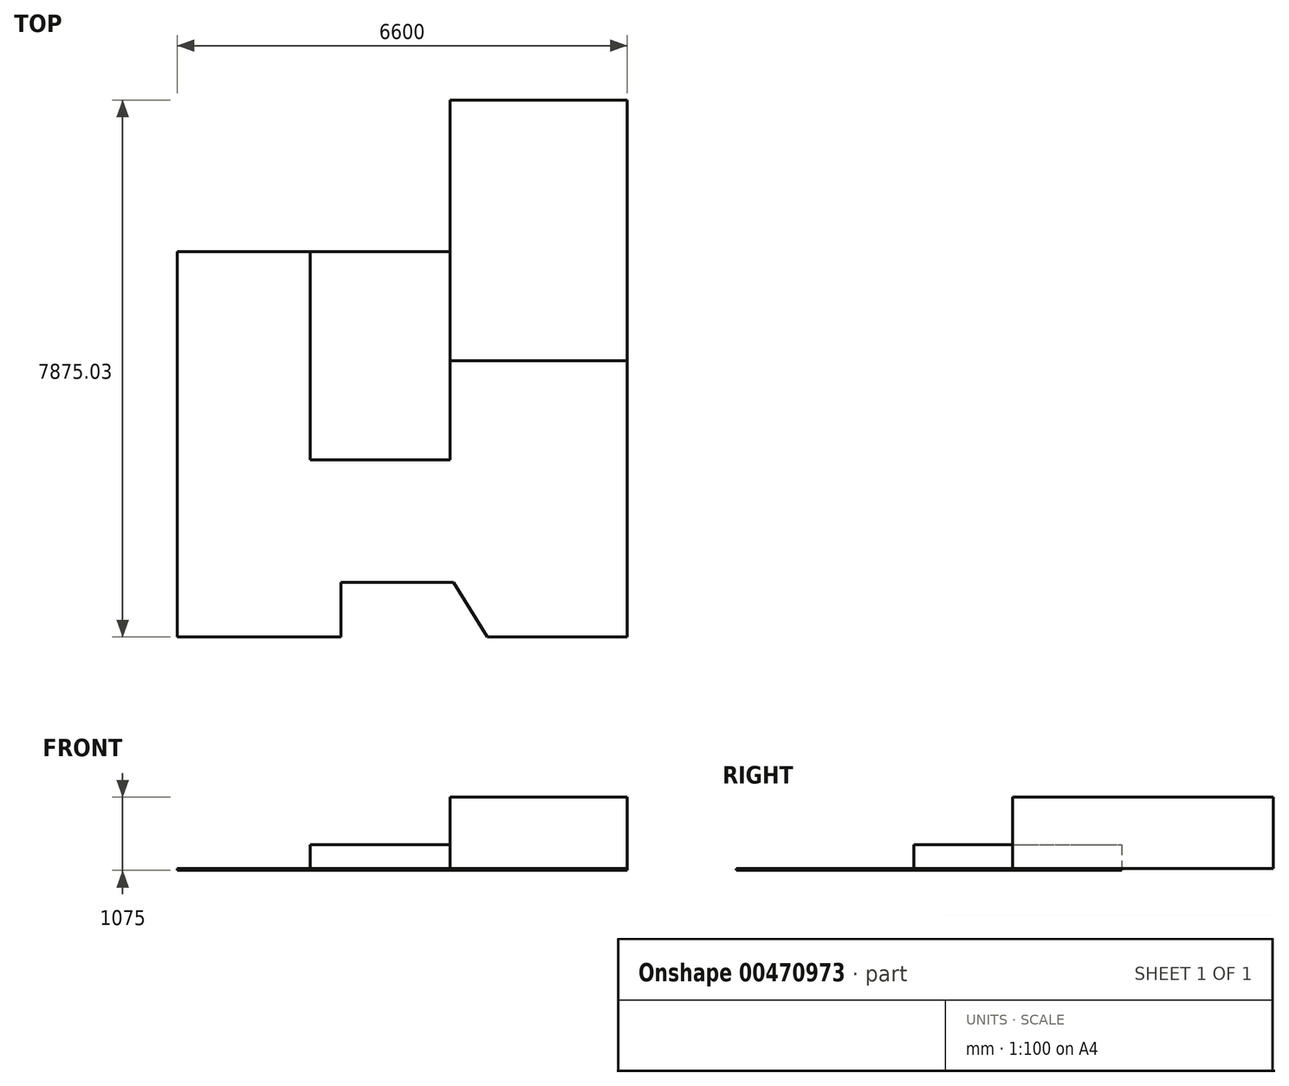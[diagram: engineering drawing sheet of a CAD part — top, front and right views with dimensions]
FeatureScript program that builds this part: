
annotation { "Feature Type Name" : "Feature", "Feature Type Description" : "" }
export const myFeature = defineFeature(function(context is Context, id is Id, definition is map)
    precondition{}
    {
        {
            var Q0;
            Q0=qCreatedBy(makeId("Top.planeOp"),FACE);
            var sketch = newSketch(context, id + "F0", { "sketchPlane" : qUnion([Q0])});
            skLineSegment(sketch, "E0.top", {"start": v(0, -12020) * mm, "end": v(2400, -12020) * mm, "construction": true});
            skLineSegment(sketch, "E0.left", {"start": v(0, 0) * mm, "end": v(0, -3400) * mm, "construction": true});
            skLineSegment(sketch, "E0.right", {"start": v(6600, -120) * mm, "end": v(6600, -12020) * mm, "construction": true});
            skLineSegment(sketch, "E1.top", {"start": v(3470, -120) * mm, "end": v(6600, -120) * mm, "construction": true});
            skLineSegment(sketch, "E2", {"start": v(0, 0) * mm, "end": v(3470, 0) * mm, "construction": true});
            skLineSegment(sketch, "E3", {"start": v(3470, -120) * mm, "end": v(3470, 0) * mm, "construction": true});
            skLineSegment(sketch, "E4.bottom", {"start": v(0, -3400) * mm, "end": v(1950, -3400) * mm, "construction": true});
            skLineSegment(sketch, "E4.top", {"start": v(0, -6120) * mm, "end": v(1950, -6120) * mm, "construction": true});
            skLineSegment(sketch, "E4.right", {"start": v(2444.97, -3894.97) * mm, "end": v(2444.97, -5625.03) * mm, "construction": true});
            skLineSegment(sketch, "E5", {"start": v(1950, -3400) * mm, "end": v(2444.97, -3894.97) * mm, "construction": true});
            skLineSegment(sketch, "E6.trimOffspring", {"start": v(0, -6120) * mm, "end": v(0, -12020) * mm, "construction": true});
            skLineSegment(sketch, "E7", {"start": v(1950, -6120) * mm, "end": v(2444.97, -5625.03) * mm, "construction": true});
            skLineSegment(sketch, "E8", {"start": v(2400, -12020) * mm, "end": v(2400, -10970) * mm, "construction": true});
            skLineSegment(sketch, "E9", {"start": v(2400, -10970) * mm, "end": v(4050, -10970) * mm, "construction": true});
            skLineSegment(sketch, "E10", {"start": v(4050, -10970) * mm, "end": v(4700, -12020) * mm, "construction": true});
            skLineSegment(sketch, "E11.trimOffspring", {"start": v(4700, -12020) * mm, "end": v(6600, -12020) * mm, "construction": true});
            skLineSegment(sketch, "E12.bottom", {"start": v(1950, -6120) * mm, "end": v(4000, -6120) * mm, "construction": true});
            skLineSegment(sketch, "E12.top", {"start": v(1950, -9170) * mm, "end": v(4000, -9170) * mm, "construction": true});
            skLineSegment(sketch, "E12.left", {"start": v(1950, -6120) * mm, "end": v(1950, -9170) * mm, "construction": true});
            skLineSegment(sketch, "E12.right", {"start": v(4000, -3894.97) * mm, "end": v(4000, -9170) * mm, "construction": true});
            skLineSegment(sketch, "E13", {"start": v(4000, -3894.97) * mm, "end": v(6600, -3894.97) * mm, "construction": true});
            skLineSegment(sketch, "E14", {"start": v(4000, -7720) * mm, "end": v(6600, -7720) * mm, "construction": true});
            skPoint(sketch, "E15", {"position": v(1950, -6120) * mm});
            skPoint(sketch, "E16", {"position": v(4000, -7720) * mm});
            skPoint(sketch, "E17", {"position": v(6600, -3894.97) * mm});
            skPoint(sketch, "E18", {"position": v(4000, -9170) * mm});
            skLineSegment(sketch, "E19", {"start": v(0, -11770) * mm, "end": v(2400, -11770) * mm, "construction": true});
            skLineSegment(sketch, "E20.trimOffspring", {"start": v(4545.24, -11770) * mm, "end": v(6600, -11770) * mm, "construction": true});
            skSolve(sketch);
        }
        {
            var Q0;
            Q0=qCreatedBy(makeId("Top.planeOp"),FACE);
            var sketch = newSketch(context, id + "F1", { "sketchPlane" : qUnion([Q0])});
            skLineSegment(sketch, "E21.bottom", {"start": v(4000, -9170) * mm, "end": v(1950, -9170) * mm});
            skLineSegment(sketch, "E21.top", {"start": v(4000, -6120) * mm, "end": v(1950, -6120) * mm});
            skLineSegment(sketch, "E21.left", {"start": v(4000, -9170) * mm, "end": v(4000, -6120) * mm});
            skLineSegment(sketch, "E21.right", {"start": v(1950, -9170) * mm, "end": v(1950, -6120) * mm});
            skSolve(sketch);
        }
        {
            var Q0;
            Q0=makeQuery(id+"F1.imprint","IMPRINT",FACE,{"disambiguationData":[TD([[makeQuery(id+"F1.imprint","IMPRINT",EDGE,{"derivedFrom":sQuery(id+"F1.wireOp",EDGE,"E21.bottom")}),-1.0]])]});
            extrude(context, id + "F2", {"entities" : qUnion([Q0]), "depth" : 350 * mm});
        }
        {
            var Q0;
            Q0=qCreatedBy(makeId("Top.planeOp"),FACE);
            var sketch = newSketch(context, id + "F3", { "sketchPlane" : qUnion([Q0])});
            skLineSegment(sketch, "E22.bottom", {"start": v(4000, -3894.97) * mm, "end": v(6600, -3894.97) * mm});
            skLineSegment(sketch, "E22.top", {"start": v(4000, -7720) * mm, "end": v(6600, -7720) * mm});
            skLineSegment(sketch, "E22.left", {"start": v(4000, -3894.97) * mm, "end": v(4000, -7720) * mm});
            skLineSegment(sketch, "E22.right", {"start": v(6600, -3894.97) * mm, "end": v(6600, -7720) * mm});
            skSolve(sketch);
        }
        {
            var Q0;
            Q0=makeQuery(id+"F3.imprint","IMPRINT",FACE,{"disambiguationData":[TD([[makeQuery(id+"F3.imprint","IMPRINT",EDGE,{"derivedFrom":sQuery(id+"F3.wireOp",EDGE,"E22.bottom")}),-1.0]])]});
            extrude(context, id + "F4", {"entities" : qUnion([Q0]), "operationType" : NewBodyOperationType.ADD, "depth" : 1050 * mm});
        }
        {
            var Q0;
            Q0=qCreatedBy(makeId("Top.planeOp"),FACE);
            var sketch = newSketch(context, id + "F5", { "sketchPlane" : qUnion([Q0])});
            skLineSegment(sketch, "E23.bottom", {"start": v(0, -6120) * mm, "end": v(1950, -6120) * mm});
            skLineSegment(sketch, "E23.top", {"start": v(0, -11770) * mm, "end": v(2400, -11770) * mm});
            skLineSegment(sketch, "E23.left", {"start": v(0, -6120) * mm, "end": v(0, -11770) * mm});
            skLineSegment(sketch, "E23.right", {"start": v(1950, -6120) * mm, "end": v(1950, -9170) * mm});
            skLineSegment(sketch, "E24", {"start": v(1950, -9170) * mm, "end": v(4000, -9170) * mm});
            skLineSegment(sketch, "E25", {"start": v(4000, -9170) * mm, "end": v(4000, -7720) * mm});
            skLineSegment(sketch, "E26", {"start": v(4000, -7720) * mm, "end": v(6600, -7720) * mm});
            skLineSegment(sketch, "E27", {"start": v(6600, -7720) * mm, "end": v(6600, -11770) * mm});
            skLineSegment(sketch, "E28", {"start": v(4545.24, -11770) * mm, "end": v(4050, -10970) * mm});
            skLineSegment(sketch, "E29", {"start": v(4050, -10970) * mm, "end": v(2400, -10970) * mm});
            skLineSegment(sketch, "E30", {"start": v(2400, -10970) * mm, "end": v(2400, -11770) * mm});
            skLineSegment(sketch, "E31", {"start": v(6600, -11770) * mm, "end": v(4545.24, -11770) * mm});
            skSolve(sketch);
        }
        {
            var Q0;
            Q0=makeQuery(id+"F5.imprint","IMPRINT",FACE,{"disambiguationData":[TD([[makeQuery(id+"F5.imprint","IMPRINT",EDGE,{"derivedFrom":sQuery(id+"F5.wireOp",EDGE,"E23.bottom")}),-1.0]])]});
            extrude(context, id + "F6", {"entities" : qUnion([Q0]), "operationType" : NewBodyOperationType.ADD, "oppositeDirection" : true, "depth" : 25 * mm});
        }
    });
